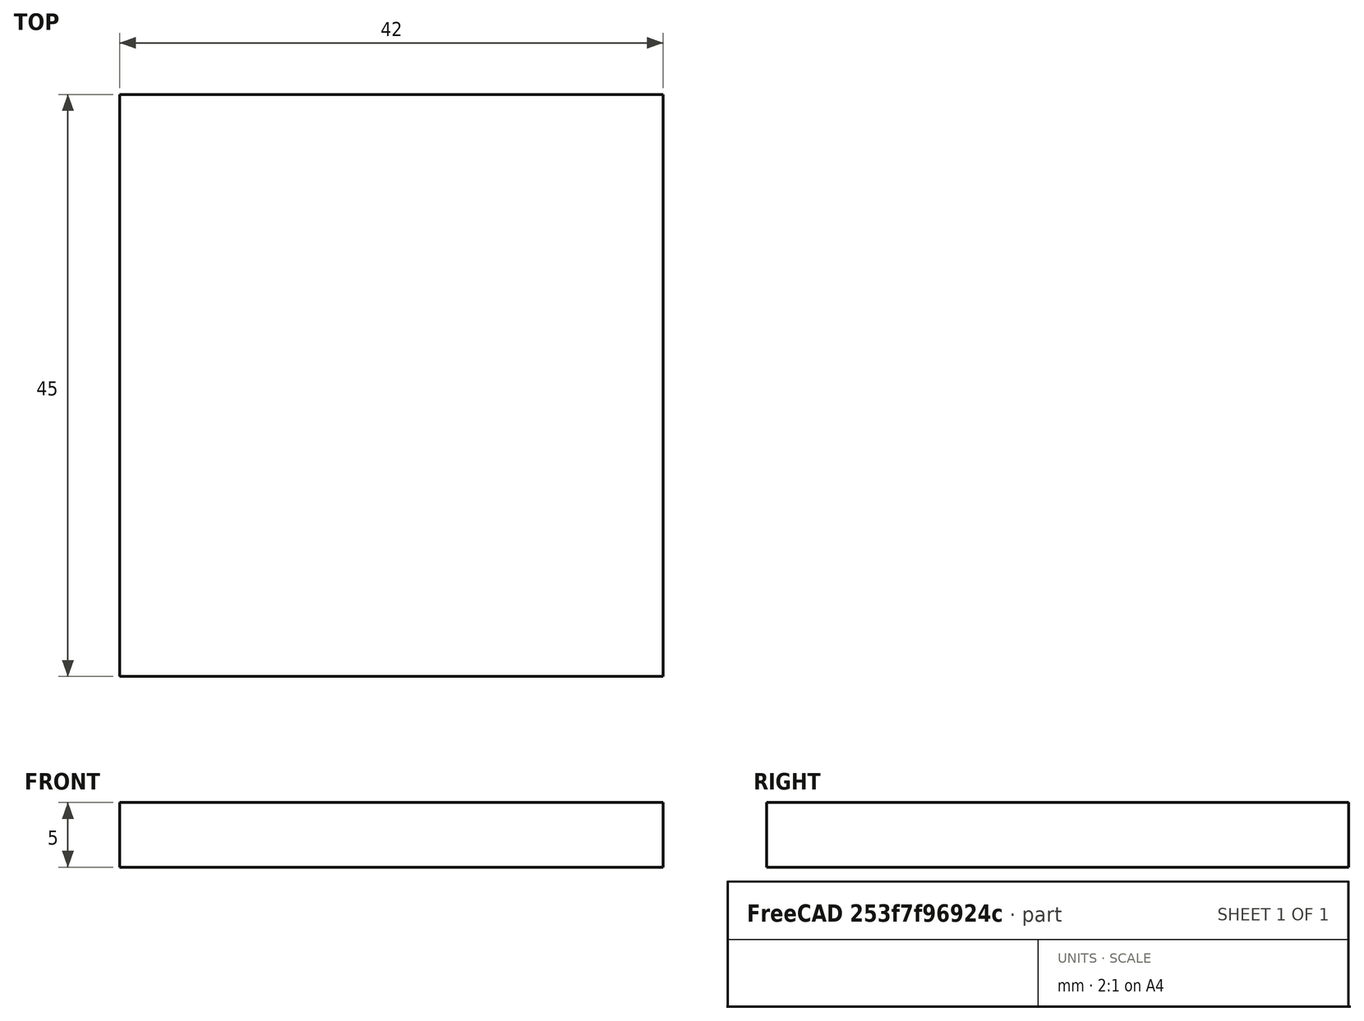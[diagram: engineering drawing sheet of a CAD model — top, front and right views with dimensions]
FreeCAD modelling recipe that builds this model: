
FCSTD DOCUMENT  (FreeCAD 0.18.3R)
Label: abrazadera_01
License: All rights reserved
LicenseURL: http://en.wikipedia.org/wiki/All_rights_reserved
objects: Path::FeaturePython×5, Sketcher::SketchObject×4, Part::FeaturePython×3, PartDesign::Pad×2, PartDesign::Pocket×2, PartDesign::Body×2, App::FeaturePython×1, App::DocumentObjectGroup×1, Path::FeatureCompoundPython×1, Mesh::FeaturePython×1
note: 20 computed .brp shape members not serialized (recipe doc carries the construction recipe); baked Part::Feature solids carry a one-line shape summary decoded from their .brp

FEATURE [Sketcher::SketchObject] Sketch
  MapMode = 5
  Support = -> [XY_Plane]
  sketch-geometry (11):
    g0: LineSegment StartX=-20 StartY=10 StartZ=0 EndX=20 EndY=10 EndZ=0
    g1: LineSegment [constr] StartX=20 StartY=10 StartZ=0 EndX=20 EndY=-10 EndZ=0
    g2: LineSegment [constr] StartX=20 StartY=-10 StartZ=0 EndX=-20 EndY=-10 EndZ=0
    g3: LineSegment [constr] StartX=-20 StartY=-10 StartZ=0 EndX=-20 EndY=10 EndZ=0
    g4: Circle CenterX=-12.5 CenterY=0 CenterZ=0 NormalX=0 NormalY=0 NormalZ=1 AngleXU=0 Radius=2.5
    g5: Circle CenterX=12.5 CenterY=0 CenterZ=0 NormalX=0 NormalY=0 NormalZ=1 AngleXU=0 Radius=2.5
    g6: LineSegment StartX=20 StartY=10 StartZ=0 EndX=20 EndY=-4 EndZ=0
    g7: LineSegment StartX=-20 StartY=10 StartZ=0 EndX=-20 EndY=-4 EndZ=0
    g8: LineSegment StartX=-5.5 StartY=-10 StartZ=0 EndX=5.5 EndY=-10 EndZ=0
    g9: ArcOfCircle CenterX=16.2216 CenterY=-15.3896 CenterZ=0 NormalX=0 NormalY=0 NormalZ=1 AngleXU=0 Radius=12 StartAngle=1.25048 EndAngle=2.6758
    g10: ArcOfCircle CenterX=-16.2216 CenterY=-15.3896 CenterZ=0 NormalX=0 NormalY=0 NormalZ=1 AngleXU=0 Radius=12 StartAngle=0.465797 EndAngle=1.89112
  constraints (31):
    c: Coincident(g0,g1)
    c: Coincident(g1,g2)
    c: Coincident(g2,g3)
    c: Coincident(g3,g0)
    c: Horizontal(g0)
    c: Horizontal(g2)
    c: Vertical(g1)
    c: Vertical(g3)
    c: Symmetric(g0,g1,g-1)
    c: DistanceX(g0,g0) = 40
    c: DistanceY(g1,g1) = 20
    c: Radius(g4) = 2.5
    c: PointOnObject(g4,g-1)
    c: DistanceX(g4,g-1) = 12.5
    c: Radius(g5) = 2.5
    c: Symmetric(g5,g4,g-2)
    c: Coincident(g6,g0)
    c: PointOnObject(g6,g1)
    c: DistanceY(g6,g5) = 4
    c: Equal(g7,g6)
    c: PointOnObject(g8,g2)
    c: Symmetric(g8,g8,g-2)
    c: Coincident(g9,g6)
    c: Equal(g9,g10)
    c: Coincident(g10,g7)
    c: Coincident(g10,g8)
    c: PointOnObject(g7,g3)
    c: DistanceX(g4,g8) = 7
    c: Coincident(g7,g0)
    c: Coincident(g9,g8)
    c: Radius(g10) = 12
FEATURE [PartDesign::Pad] Pad
  Length = 5
  Length2 = 100
  Profile = -> Sketch
  Refine = true
  Reversed = true
  Type = 0
FEATURE [Sketcher::SketchObject] Sketch001
  MapMode = 5
  Support = -> [Pad]
  sketch-geometry (8):
    g0: LineSegment StartX=-6.5 StartY=-2.25 StartZ=0 EndX=6.5 EndY=-2.25 EndZ=0
    g1: LineSegment StartX=6.5 StartY=-2.25 StartZ=0 EndX=6.5 EndY=-8.25 EndZ=0
    g2: LineSegment StartX=6.5 StartY=-8.25 StartZ=0 EndX=-6.5 EndY=-8.25 EndZ=0
    g3: LineSegment StartX=-6.5 StartY=-8.25 StartZ=0 EndX=-6.5 EndY=-2.25 EndZ=0
    g4: LineSegment StartX=-6.5 StartY=6.75 StartZ=0 EndX=6.5 EndY=6.75 EndZ=0
    g5: LineSegment StartX=6.5 StartY=6.75 StartZ=0 EndX=6.5 EndY=2.25 EndZ=0
    g6: LineSegment StartX=6.5 StartY=2.25 StartZ=0 EndX=-6.5 EndY=2.25 EndZ=0
    g7: LineSegment StartX=-6.5 StartY=2.25 StartZ=0 EndX=-6.5 EndY=6.75 EndZ=0
  constraints (21):
    c: Coincident(g0,g1)
    c: Coincident(g1,g2)
    c: Coincident(g2,g3)
    c: Coincident(g3,g0)
    c: Horizontal(g0)
    c: Vertical(g1)
    c: DistanceX(g2,g2) = 13
    c: Symmetric(g1,g2,g-2)
    c: DistanceY(g0,g-1) = 2.25
    c: DistanceY(g1,g1) = 6
    c: Coincident(g4,g5)
    c: Coincident(g5,g6)
    c: Coincident(g6,g7)
    c: Coincident(g7,g4)
    c: Horizontal(g4)
    c: Vertical(g5)
    c: Vertical(g7)
    c: Symmetric(g5,g6,g-2)
    c: Symmetric(g6,g0,g-1)
    c: Equal(g6,g0)
    c: DistanceY(g5,g5) = 4.5
FEATURE [PartDesign::Pocket] Pocket
  BaseFeature = -> Pad
  Length = 2.5
  Length2 = 100
  Profile = -> Sketch001
  Refine = true
  Type = 0
FEATURE [PartDesign::Body] Body  label="back"
  Group = -> [Sketch,Pad,Sketch001,Pocket]
  Origin = -> Origin
  Tip = -> Pocket
FEATURE [Sketcher::SketchObject] Sketch002
  MapMode = 5
  Support = -> [XY_Plane001]
  sketch-geometry (7):
    g0: LineSegment StartX=-20 StartY=33 StartZ=0 EndX=20 EndY=33 EndZ=0
    g1: LineSegment StartX=20 StartY=33 StartZ=0 EndX=20 EndY=13 EndZ=0
    g2: LineSegment StartX=20 StartY=13 StartZ=0 EndX=-20 EndY=13 EndZ=0
    g3: LineSegment StartX=-20 StartY=13 StartZ=0 EndX=-20 EndY=33 EndZ=0
    g4: LineSegment [constr] StartX=-20 StartY=23 StartZ=0 EndX=20 EndY=23 EndZ=0
    g5: Circle CenterX=-12.5 CenterY=23 CenterZ=0 NormalX=0 NormalY=0 NormalZ=1 AngleXU=0 Radius=2.5
    g6: Circle CenterX=12.5 CenterY=23 CenterZ=0 NormalX=0 NormalY=0 NormalZ=1 AngleXU=0 Radius=2.5
  constraints (19):
    c: Coincident(g0,g1)
    c: Coincident(g1,g2)
    c: Coincident(g2,g3)
    c: Coincident(g3,g0)
    c: Horizontal(g0)
    c: Vertical(g1)
    c: Vertical(g3)
    c: DistanceY(g3,g3) = 20
    c: DistanceX(g0,g0) = 40
    c: Symmetric(g2,g1,g-2)
    c: DistanceY(g-1,g2) = 13
    c: PointOnObject(g4,g1)
    c: Horizontal(g4)
    c: Symmetric(g2,g0,g4)
    c: PointOnObject(g5,g4)
    c: Radius(g5) = 2.5
    c: Radius(g6) = 2.5
    c: Symmetric(g6,g5,g-2)
    c: DistanceX(g5,g-1) = 12.5
FEATURE [PartDesign::Pad] Pad001
  Length = 5
  Length2 = 100
  Profile = -> Sketch002
  Refine = true
  Reversed = true
  Type = 0
FEATURE [Sketcher::SketchObject] Sketch003
  ExternalGeometry = -> [Pad001]
  MapMode = 5
  Support = -> [Pad001]
  sketch-geometry (9):
    g0: LineSegment [constr] StartX=-20 StartY=23 StartZ=0 EndX=20 EndY=23 EndZ=0
    g1: LineSegment StartX=-6.5 StartY=20.75 StartZ=0 EndX=6.5 EndY=20.75 EndZ=0
    g2: LineSegment StartX=6.5 StartY=20.75 StartZ=0 EndX=6.5 EndY=14.75 EndZ=0
    g3: LineSegment StartX=6.5 StartY=14.75 StartZ=0 EndX=-6.5 EndY=14.75 EndZ=0
    g4: LineSegment StartX=-6.5 StartY=14.75 StartZ=0 EndX=-6.5 EndY=20.75 EndZ=0
    g5: LineSegment StartX=-6.5 StartY=29.75 StartZ=0 EndX=6.5 EndY=29.75 EndZ=0
    g6: LineSegment StartX=6.5 StartY=29.75 StartZ=0 EndX=6.5 EndY=25.25 EndZ=0
    g7: LineSegment StartX=6.5 StartY=25.25 StartZ=0 EndX=-6.5 EndY=25.25 EndZ=0
    g8: LineSegment StartX=-6.5 StartY=25.25 StartZ=0 EndX=-6.5 EndY=29.75 EndZ=0
  constraints (24):
    c: PointOnObject(g0,g-4)
    c: Horizontal(g0)
    c: Symmetric(g-3,g-3,g0)
    c: Coincident(g1,g2)
    c: Coincident(g2,g3)
    c: Coincident(g3,g4)
    c: Coincident(g4,g1)
    c: Horizontal(g1)
    c: Vertical(g2)
    c: DistanceY(g2,g2) = 6
    c: Symmetric(g2,g3,g-2)
    c: DistanceX(g1,g1) = 13
    c: DistanceY(g1,g0) = 2.25
    c: Coincident(g5,g6)
    c: Coincident(g6,g7)
    c: Coincident(g7,g8)
    c: Coincident(g8,g5)
    c: Horizontal(g5)
    c: Vertical(g6)
    c: Vertical(g8)
    c: Equal(g7,g1)
    c: Symmetric(g7,g6,g-2)
    c: Symmetric(g7,g1,g0)
    c: DistanceY(g6,g6) = 4.5
FEATURE [PartDesign::Pocket] Pocket001
  BaseFeature = -> Pad001
  Length = 2.5
  Length2 = 100
  Profile = -> Sketch003
  Refine = true
  Type = 0
FEATURE [PartDesign::Body] Body001  label="front"
  Group = -> [Sketch002,Pad001,Sketch003,Pocket001]
  Origin = -> Origin001
  Tip = -> Pocket001
FEATURE [App::FeaturePython] SetupSheet  # Path/CAM operation (typed FeaturePython)
  ClearanceHeightExpression = OpStockZMax+SetupSheet.ClearanceHeightOffset
  ClearanceHeightOffset = 3
  FinalDepthExpression = -5
  HorizRapid = 5
  SafeHeightExpression = OpStockZMax+SetupSheet.SafeHeightOffset
  SafeHeightOffset = 3
  StartDepthExpression = 0
  StepDownExpression = 1.7
  VertRapid = 4
FEATURE [Part::FeaturePython] Clone  label="Model-back"  # Draft clone (typed FeaturePython)
  AttacherType = Attacher::AttachEngine3D
  Fuse = false
  Objects = -> [Body]
  PathResource = Model
  Scale = (1,1,1)
FEATURE [Part::FeaturePython] Clone001  label="Model-front"  # Draft clone (typed FeaturePython)
  AttacherType = Attacher::AttachEngine3D
  Fuse = false
  Objects = -> [Body001]
  PathResource = Model
  Scale = (1,1,1)
FEATURE [App::DocumentObjectGroup] Model
  Group = -> [Clone,Clone001]
FEATURE [Path::FeaturePython] Default_Tool  label="Endmill 3mm"  # Path/CAM operation (typed FeaturePython)
  HorizFeed = 0.8
  HorizRapid = 5
  SpindleDir = 0
  SpindleSpeed = 0
  ToolNumber = 1
  VertFeed = 0.5
  VertRapid = 4
  expr: HorizRapid = SetupSheet.HorizRapid
  expr: VertRapid = SetupSheet.VertRapid
FEATURE [Part::FeaturePython] Stock  # WARN: FeaturePython — macro-defined, semantics opaque (R4)
  Base = -> Model
  ExtXneg = 1
  ExtXpos = 1
  ExtYneg = 1
  ExtYpos = 1
  ExtZneg = 0
  ExtZpos = 0
  Placement = pos=(-20,-10,-5) rot=(0,0,1;0rad)
  StockType = FromBase
FEATURE [Path::FeaturePython] Profile_Edges  label="Agujeros"  # Path/CAM operation (typed FeaturePython)
  Active = true
  AreaParams:
    Tolerance = 1e-07
    FitArcs = True
    Simplify = False
    CleanDistance = 0.0
    Accuracy = 0.01
    Unit = 1.0
    MinArcPoints = 4
    MaxArcPoints = 100
    ClipperScale = 10000000.0
    Fill = 0
    Coplanar = 0
    Reorient = True
    Outline = False
    Explode = False
    OpenMode = 0
    Deflection = 0.01
    SubjectFill = 0
    ClipFill = 0
    Offset = -1.5
    ExtraPass = 0
    Stepover = 0.0
    LastStepover = 0.0
    JoinType = 0
    EndType = 0
    MiterLimit = 2.0
    RoundPrecision = 0.0
    PocketMode = 0
    ToolRadius = 1.0
    PocketExtraOffset = 0.0
    PocketStepover = 0.0
    PocketLastStepover = 0.0
    FromCenter = False
    Angle = 45.0
    AngleShift = 0.0
    Shift = 0.0
    Thicken = False
    SectionCount = -1
    Stepdown = 1.0
    SectionOffset = 0.0
    SectionTolerance = 1e-06
    SectionMode = 2
    Project = False
  Base = -> [Clone,Clone001]
  ClearanceHeight = 3
  Direction = 0
  FinalDepth = -5
  JoinType = 0
  MiterLimit = 0.1
  OffsetExtra = 0
  OpFinalDepth = 0
  OpStartDepth = 1.7
  OpStockZMax = 0
  OpStockZMin = -5
  OpToolDiameter = 3
  PathParams = {'orientation': 1, 'feedrate': 0.8, 'feedrate_v': 0.5, 'verbose': True, 'resume_height': 3.0, 'retraction': 3.0, 'return_end': True, 'preamble': False}
  SafeHeight = 3
  Side = 1
  StartDepth = 0
  StartPoint = (0,0,0)
  StepDown = 1.7
  ToolController = -> Default_Tool
  UseComp = true
  UseStartPoint = false
  expr: ClearanceHeight = OpStockZMax + SetupSheet.ClearanceHeightOffset
  expr: SafeHeight = OpStockZMax + SetupSheet.SafeHeightOffset
  expr: StepDown = 1.7
  expr: FinalDepth = -5
  expr: StartDepth = 0
FEATURE [Path::FeaturePython] Pocket_3D  label="Ranuras"  # Path/CAM operation (typed FeaturePython)
  Active = true
  AreaParams:
    Tolerance = 1e-07
    FitArcs = True
    Simplify = False
    CleanDistance = 0.0
    Accuracy = 0.01
    Unit = 1.0
    MinArcPoints = 4
    MaxArcPoints = 100
    ClipperScale = 10000000.0
    Fill = 0
    Coplanar = 0
    Reorient = True
    Outline = False
    Explode = False
    OpenMode = 0
    Deflection = 0.01
    SubjectFill = 0
    ClipFill = 0
    Offset = 0.0
    ExtraPass = 0
    Stepover = 0.0
    LastStepover = 0.0
    JoinType = 0
    EndType = 0
    MiterLimit = 2.0
    RoundPrecision = 0.0
    PocketMode = 2
    ToolRadius = 1.5
    PocketExtraOffset = 0.0
    PocketStepover = 3.0
    PocketLastStepover = 0.0
    FromCenter = True
    Angle = 45.0
    AngleShift = 0.0
    Shift = 0.0
    Thicken = False
    SectionCount = -1
    Stepdown = 1.0
    SectionOffset = 0.0
    SectionTolerance = 1e-06
    SectionMode = 2
    Project = False
  Base = -> [Clone001,Clone]
  ClearanceHeight = 3
  CutMode = 0
  ExtraOffset = 0
  FinalDepth = -5
  FinishDepth = 0
  KeepToolDown = false
  MinTravel = false
  OffsetPattern = 1
  OpFinalDepth = -2.5
  OpStartDepth = 0
  OpStockZMax = 0
  OpStockZMin = -5
  OpToolDiameter = 3
  PathParams = {'orientation': 1, 'feedrate': 0.8, 'feedrate_v': 0.5, 'verbose': True, 'resume_height': 3.0, 'retraction': 3.0, 'return_end': True, 'preamble': False}
  SafeHeight = 3
  StartAt = 0
  StartDepth = 0
  StartPoint = (0,0,0)
  StepDown = 1.7
  StepOver = 100
  ToolController = -> Default_Tool
  UseStartPoint = false
  ZigZagAngle = 45
  expr: ClearanceHeight = OpStockZMax + SetupSheet.ClearanceHeightOffset
  expr: SafeHeight = OpStockZMax + SetupSheet.SafeHeightOffset
  expr: StepDown = 1.7
  expr: FinalDepth = -5
  expr: StartDepth = 0
FEATURE [Path::FeaturePython] Contour  # Path/CAM operation (typed FeaturePython)
  Active = true
  AreaParams:
    Tolerance = 1e-07
    FitArcs = True
    Simplify = False
    CleanDistance = 0.0
    Accuracy = 0.01
    Unit = 1.0
    MinArcPoints = 4
    MaxArcPoints = 100
    ClipperScale = 10000000.0
    Fill = 0
    Coplanar = 2
    Reorient = True
    Outline = False
    Explode = False
    OpenMode = 0
    Deflection = 0.01
    SubjectFill = 0
    ClipFill = 0
    Offset = 1.5
    ExtraPass = 0
    Stepover = 0.0
    LastStepover = 0.0
    JoinType = 0
    EndType = 0
    MiterLimit = 2.0
    RoundPrecision = 0.0
    PocketMode = 0
    ToolRadius = 1.0
    PocketExtraOffset = 0.0
    PocketStepover = 0.0
    PocketLastStepover = 0.0
    FromCenter = False
    Angle = 45.0
    AngleShift = 0.0
    Shift = 0.0
    Thicken = False
    SectionCount = -1
    Stepdown = 1.0
    SectionOffset = 0.0
    SectionTolerance = 1e-06
    SectionMode = 2
    Project = False
  ClearanceHeight = 3
  Direction = 0
  FinalDepth = -5
  JoinType = 0
  MiterLimit = 0.1
  OffsetExtra = 0
  OpFinalDepth = -5
  OpStartDepth = 0
  OpStockZMax = 0
  OpStockZMin = -5
  OpToolDiameter = 3
  PathParams = {'orientation': 1, 'feedrate': 0.8, 'feedrate_v': 0.5, 'verbose': True, 'resume_height': 3.0, 'retraction': 3.0, 'return_end': True, 'preamble': False}
  SafeHeight = 3
  Side = 0
  StartDepth = 0
  StartPoint = (0,0,0)
  StepDown = 1.7
  ToolController = -> Default_Tool
  UseComp = true
  UseStartPoint = false
  expr: ClearanceHeight = OpStockZMax + SetupSheet.ClearanceHeightOffset
  expr: SafeHeight = OpStockZMax + SetupSheet.SafeHeightOffset
  expr: StepDown = 1.7
  expr: FinalDepth = -5
  expr: StartDepth = 0
FEATURE [Path::FeatureCompoundPython] Operations  # Path/CAM operation (typed FeaturePython)
  Group = -> [Profile_Edges,Pocket_3D,Contour]
  UsePlacements = false
FEATURE [Path::FeaturePython] Job  label="Fresado"  # Path/CAM operation (typed FeaturePython)
  GeometryTolerance = 0.01
  Model = -> Model
  Operations = -> Operations
  PostProcessor = 1
  SetupSheet = -> SetupSheet
  Stock = -> Stock
  ToolController = -> [Default_Tool]
FEATURE [Mesh::FeaturePython] CutMaterial  # WARN: FeaturePython — macro-defined, semantics opaque (R4)
